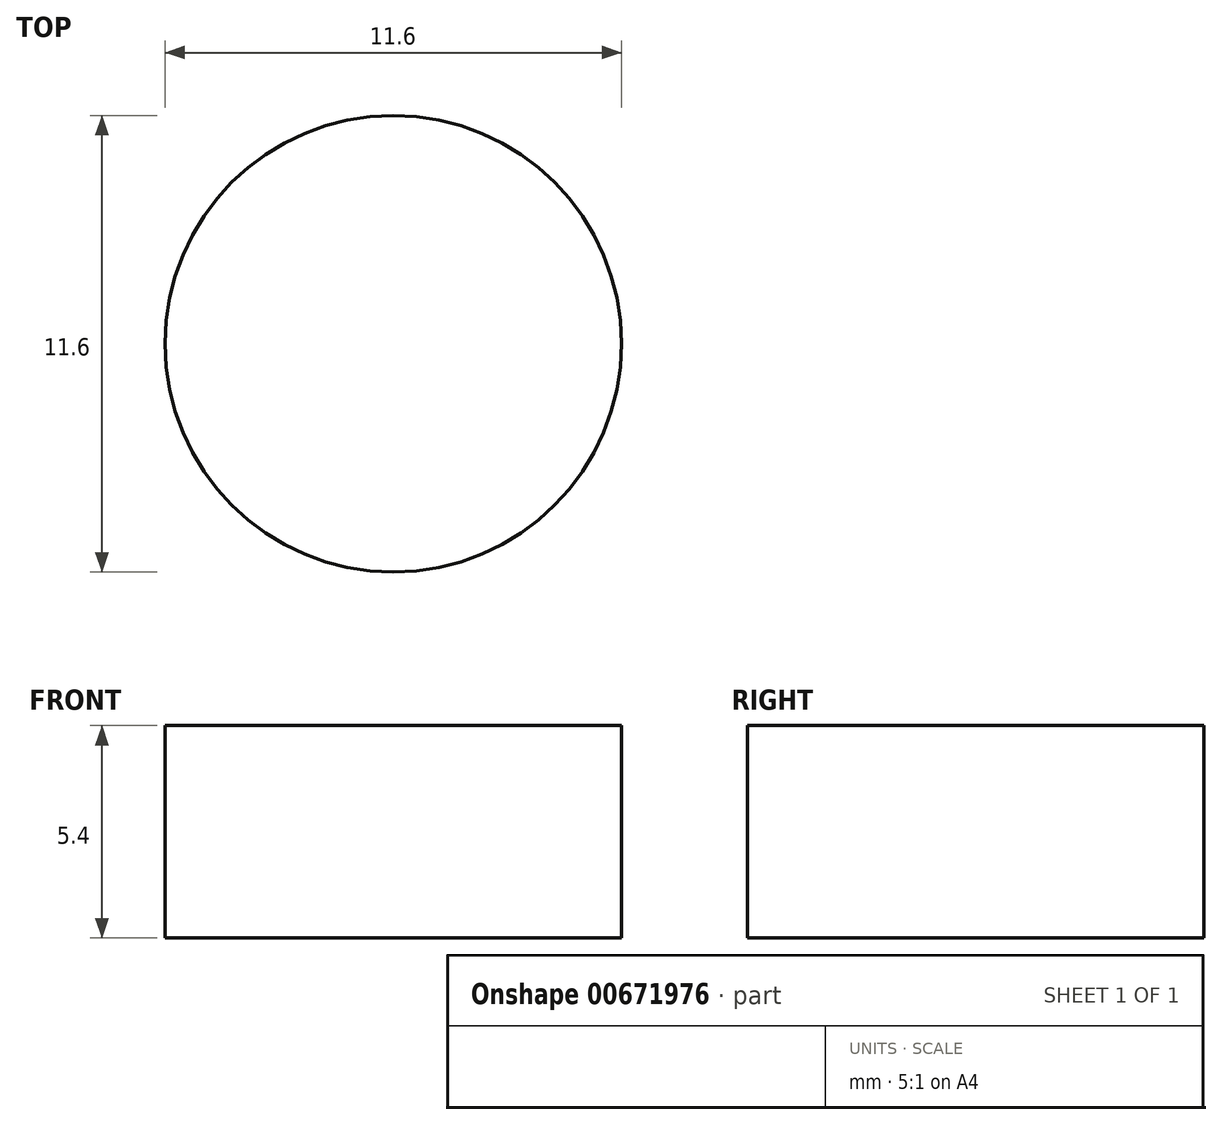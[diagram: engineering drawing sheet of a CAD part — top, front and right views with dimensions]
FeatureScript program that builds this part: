
annotation { "Feature Type Name" : "Feature", "Feature Type Description" : "" }
export const myFeature = defineFeature(function(context is Context, id is Id, definition is map)
    precondition{}
    {
        {
            var Q0;
            Q0=qCreatedBy(makeId("Top.planeOp"),FACE);
            var sketch = newSketch(context, id + "F0", { "sketchPlane" : qUnion([Q0])});
            skCircle(sketch, "E0", {"center": v(0, 0) * mm, "radius": 5.8 * mm});
            skSolve(sketch);
        }
        {
            var Q0;
            Q0 = qSketchRegion(id + "F0", true);
            extrude(context, id + "F1", {"entities" : qUnion([Q0]), "depth" : 5.4 * mm, "offsetDistance" : 25 * mm});
        }
    });
